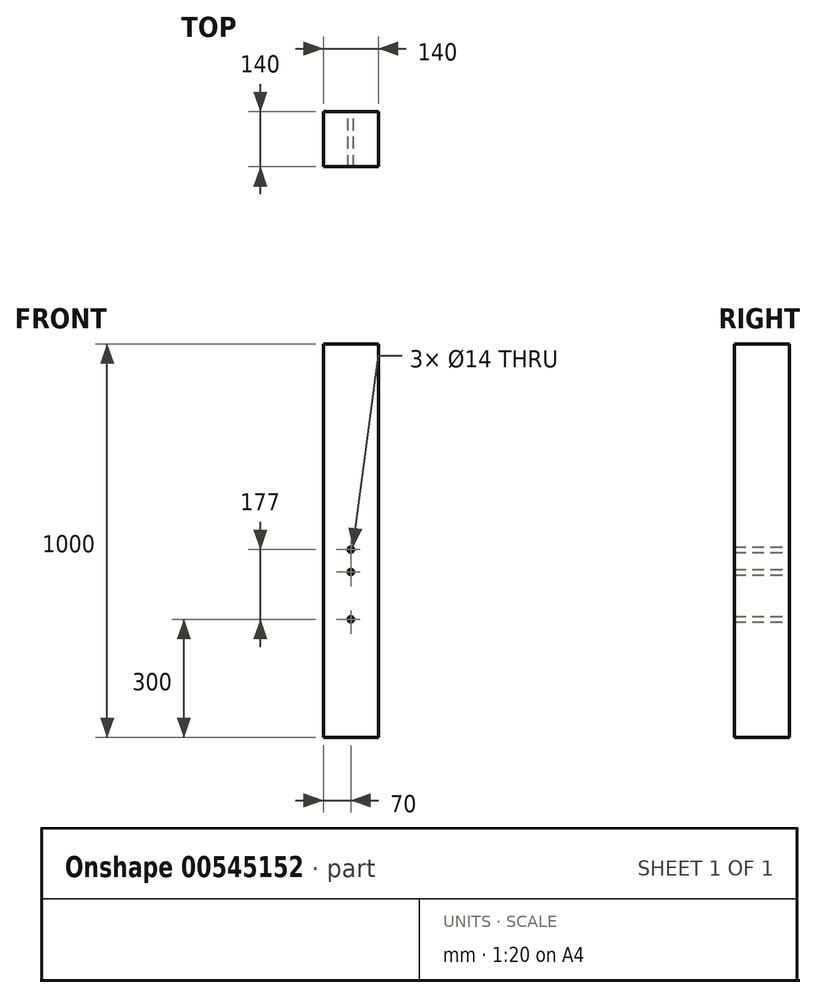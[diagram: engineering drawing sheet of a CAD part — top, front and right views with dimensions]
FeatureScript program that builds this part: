
annotation { "Feature Type Name" : "Feature", "Feature Type Description" : "" }
export const myFeature = defineFeature(function(context is Context, id is Id, definition is map)
    precondition{}
    {
        {
            var Q0;
            Q0=qCreatedBy(makeId("Front.planeOp"),FACE);
            var sketch = newSketch(context, id + "F0", { "sketchPlane" : qUnion([Q0])});
            skLineSegment(sketch, "E0.bottom", {"start": v(70, -500) * mm, "end": v(-70, -500) * mm});
            skLineSegment(sketch, "E0.top", {"start": v(70, 500) * mm, "end": v(-70, 500) * mm});
            skLineSegment(sketch, "E0.left", {"start": v(70, -500) * mm, "end": v(70, 500) * mm});
            skLineSegment(sketch, "E0.right", {"start": v(-70, -500) * mm, "end": v(-70, 500) * mm});
            skPoint(sketch, "E0.middle", {"position": v(0, 0) * mm});
            skCircle(sketch, "E1", {"center": v(0, -200) * mm, "radius": 7 * mm});
            skCircle(sketch, "E2", {"center": v(0, -80) * mm, "radius": 7 * mm});
            skCircle(sketch, "E3", {"center": v(0, -23) * mm, "radius": 7 * mm});
            skSolve(sketch);
        }
        {
            var Q0;
            Q0 = qSketchRegion(id + "F0", true);
            extrude(context, id + "F1", {"entities" : qUnion([Q0]), "depth" : 140 * mm, "offsetDistance" : 25 * mm});
        }
    });
